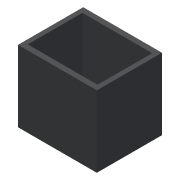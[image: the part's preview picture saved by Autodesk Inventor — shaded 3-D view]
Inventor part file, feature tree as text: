
AUTODESK INVENTOR PART (.ipt)
format: ipt  version: 2016 SP2 (Build 200236200, 236)  size: 91,648 bytes
history: native  units: mm
features: extrude x2, sketch x2
ambient origin geometry x8: Origin, YZ Plane, XZ Plane, XY Plane, X Axis, Y Axis, Z Axis, Center Point
bodies: Body1 (feature_tree)
feature tree (4):
  extrude  "Extrusion3"  Depth=508.0mm
  extrude  "Extrusion4"  Depth=450.0mm
  sketch  "Sketch1"  dims[d4=420.0mm d5=508.0mm]
  sketch  "Sketch2"  dims[d6=459.994mm d7=0.0mm d8=450.0mm d9=352.0mm d10=459.994mm d11=0.0mm]
